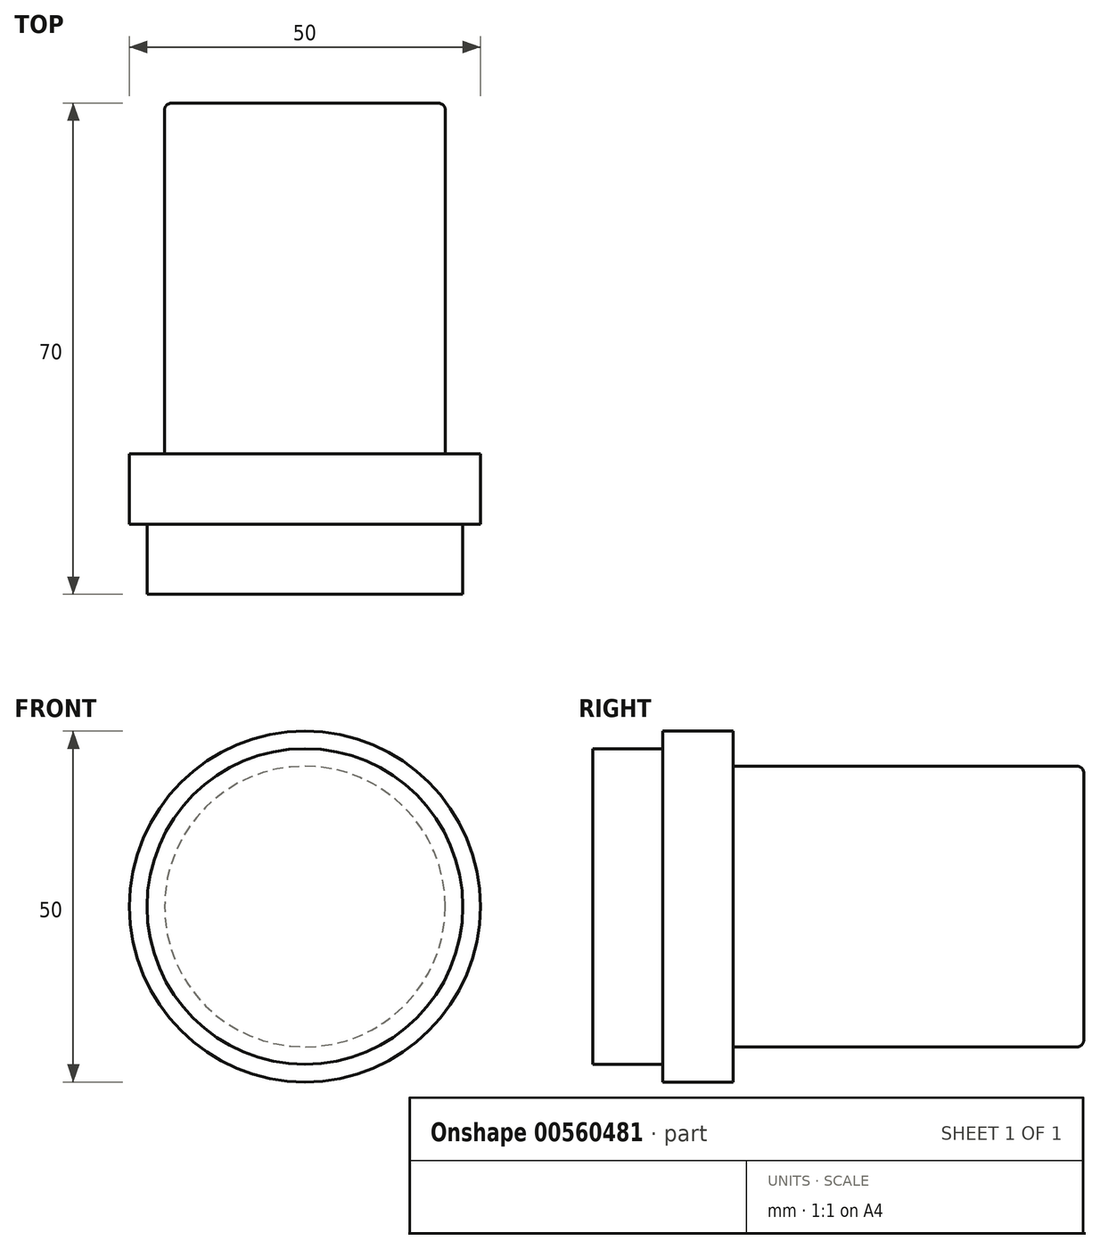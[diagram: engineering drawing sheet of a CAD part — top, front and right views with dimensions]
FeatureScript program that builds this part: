
annotation { "Feature Type Name" : "Feature", "Feature Type Description" : "" }
export const myFeature = defineFeature(function(context is Context, id is Id, definition is map)
    precondition{}
    {
        {
            var Q0;
            Q0=qCreatedBy(makeId("Front.planeOp"),FACE);
            var sketch = newSketch(context, id + "F0", { "sketchPlane" : qUnion([Q0])});
            skCircle(sketch, "E0", {"center": v(0, 0) * mm, "radius": 20 * mm});
            skSolve(sketch);
        }
        {
            var Q0;
            Q0=makeQuery(id+"F0.imprint","IMPRINT",FACE,{"disambiguationData":[TD([[makeQuery(id+"F0.imprint","IMPRINT",EDGE,{"derivedFrom":sQuery(id+"F0.wireOp",EDGE,"E0")}),1.0]])]});
            extrude(context, id + "F1", {"entities" : qUnion([Q0]), "depth" : 50 * mm, "offsetDistance" : 25 * mm});
        }
        {
            var Q0;
            Q0=makeQuery(id+"F1.opExtrude","CAP_FACE",FACE,{"disambiguationData":[OSD([sQuery(id+"F0.wireOp",EDGE,"E0")])],"isStart":false});
            var sketch = newSketch(context, id + "F2", { "sketchPlane" : qUnion([Q0])});
            skCircle(sketch, "E1", {"center": v(0, 0) * mm, "radius": 25 * mm});
            skSolve(sketch);
        }
        {
            var Q0;
            Q0 = qSketchRegion(id + "F2", true);
            extrude(context, id + "F3", {"entities" : qUnion([Q0]), "operationType" : NewBodyOperationType.ADD, "depth" : 10 * mm, "offsetDistance" : 25 * mm});
        }
        {
            var Q0;
            Q0=makeQuery(id+"F3.opExtrude","CAP_FACE",FACE,{"disambiguationData":[OSD([sQuery(id+"F2.wireOp",EDGE,"E1")])],"isStart":false});
            var sketch = newSketch(context, id + "F4", { "sketchPlane" : qUnion([Q0])});
            skCircle(sketch, "E2", {"center": v(0, 0) * mm, "radius": 22.5 * mm});
            skSolve(sketch);
        }
        {
            var Q0;
            Q0=makeQuery(id+"F4.imprint","IMPRINT",FACE,{"disambiguationData":[TD([[makeQuery(id+"F4.imprint","IMPRINT",EDGE,{"derivedFrom":sQuery(id+"F4.wireOp",EDGE,"E2")}),1.0]])]});
            extrude(context, id + "F5", {"entities" : qUnion([Q0]), "operationType" : NewBodyOperationType.ADD, "depth" : 10 * mm, "offsetDistance" : 25 * mm});
        }
        {
            var Q0;
            Q0=makeQuery(id+"F1.opExtrude","CAP_FACE",FACE,{"disambiguationData":[OSD([sQuery(id+"F0.wireOp",EDGE,"E0")])],"isStart":true});
            fillet(context, id + "F6", {"entities" : qUnion([Q0]), "radius" : 1 * mm, "tangentPropagation" : true, "allowEdgeOverflow" : false});
        }
    });
